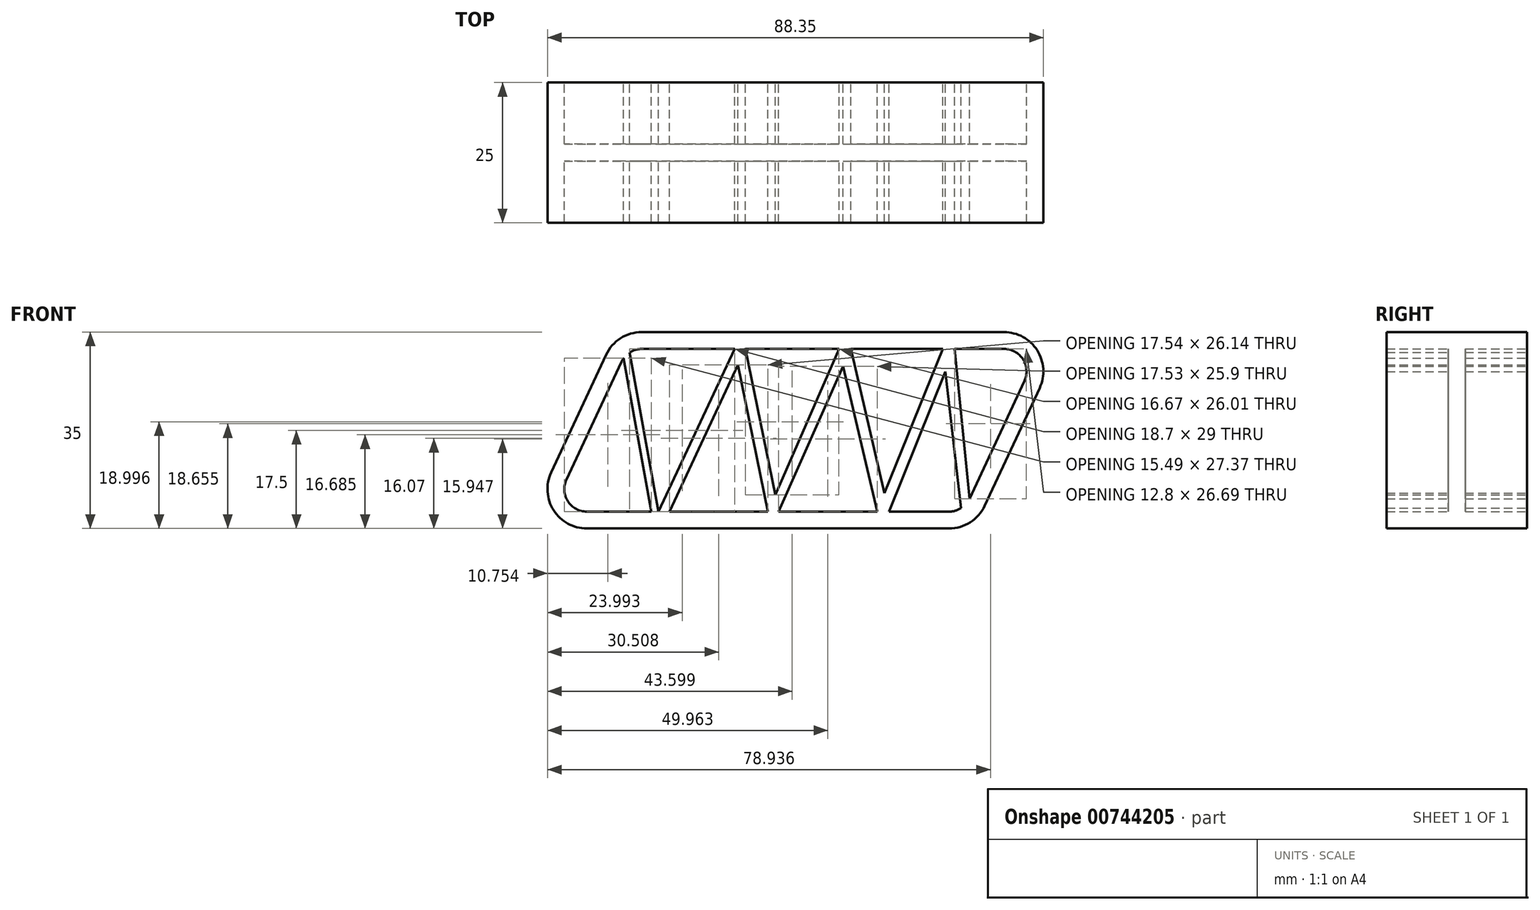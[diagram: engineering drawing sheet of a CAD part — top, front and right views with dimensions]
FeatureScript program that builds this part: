
annotation { "Feature Type Name" : "Feature", "Feature Type Description" : "" }
export const myFeature = defineFeature(function(context is Context, id is Id, definition is map)
    precondition{}
    {
        {
            var Q0;
            Q0=qCreatedBy(makeId("Front.planeOp"),FACE);
            var sketch = newSketch(context, id + "F0", { "sketchPlane" : qUnion([Q0])});
            skLineSegment(sketch, "E0", {"start": v(-27.29, -2) * mm, "end": v(37.26, -2) * mm});
            skLineSegment(sketch, "E1", {"start": v(43.6, 2.04) * mm, "end": v(53.4, 23.04) * mm});
            skLineSegment(sketch, "E2", {"start": v(47.06, 33) * mm, "end": v(-17.5, 33) * mm});
            skLineSegment(sketch, "E3", {"start": v(-23.84, 28.96) * mm, "end": v(-33.63, 7.96) * mm});
            skArc(sketch, "E4.filletArc", {"start": v(-33.63, 7.96) * mm, "mid": v(-33.2, 1.24) * mm, "end": v(-27.29, -2) * mm});
            skArc(sketch, "E5.filletArc", {"start": v(37.26, -2) * mm, "mid": v(41.02, -0.9) * mm, "end": v(43.6, 2.04) * mm});
            skPoint(sketch, "E6.visualSharp", {"position": v(53.33, 32) * mm});
            skPoint(sketch, "E7.visualSharp", {"position": v(58.04, 33) * mm});
            skArc(sketch, "E7.filletArc", {"start": v(53.4, 23.04) * mm, "mid": v(52.96, 29.76) * mm, "end": v(47.06, 33) * mm});
            skPoint(sketch, "E8.visualSharp", {"position": v(-21.96, 33) * mm});
            skArc(sketch, "E8.filletArc", {"start": v(-17.5, 33) * mm, "mid": v(-21.26, 31.9) * mm, "end": v(-23.84, 28.96) * mm});
            skArc(sketch, "E9.0", {"start": v(50.68, 24.3) * mm, "mid": v(50.43, 28.15) * mm, "end": v(47.06, 30) * mm});
            skLineSegment(sketch, "E9.1", {"start": v(40.89, 3.3) * mm, "end": v(50.68, 24.3) * mm});
            skLineSegment(sketch, "E9.2", {"start": v(47.06, 30) * mm, "end": v(38.24, 30) * mm});
            skArc(sketch, "E9.3", {"start": v(37.26, 1) * mm, "mid": v(38.38, 1.16) * mm, "end": v(39.41, 1.63) * mm});
            skArc(sketch, "E9.4", {"start": v(-17.5, 30) * mm, "mid": v(-18.62, 29.84) * mm, "end": v(-19.65, 29.37) * mm});
            skLineSegment(sketch, "E9.5", {"start": v(-21.12, 27.7) * mm, "end": v(-30.91, 6.7) * mm});
            skArc(sketch, "E9.6", {"start": v(-30.91, 6.7) * mm, "mid": v(-30.66, 2.85) * mm, "end": v(-27.29, 1) * mm});
            skLineSegment(sketch, "E9.7", {"start": v(-27.29, 1) * mm, "end": v(-15.8, 1) * mm});
            skLineSegment(sketch, "E10", {"start": v(-19.65, 29.37) * mm, "end": v(-14.54, 1) * mm});
            skLineSegment(sketch, "E11", {"start": v(-14.54, 1) * mm, "end": v(-0.95, 30) * mm});
            skLineSegment(sketch, "E12", {"start": v(-0.36, 27.14) * mm, "end": v(4.99, 1) * mm});
            skLineSegment(sketch, "E13", {"start": v(6.3, 4) * mm, "end": v(17.65, 30) * mm});
            skLineSegment(sketch, "E14", {"start": v(18.37, 26.9) * mm, "end": v(24.44, 1) * mm});
            skLineSegment(sketch, "E15", {"start": v(25.77, 4.3) * mm, "end": v(36.14, 30) * mm});
            skLineSegment(sketch, "E16", {"start": v(36.6, 25.95) * mm, "end": v(39.41, 1.63) * mm});
            skLineSegment(sketch, "E17", {"start": v(-15.8, 1) * mm, "end": v(-20.72, 28.37) * mm});
            skLineSegment(sketch, "E18", {"start": v(-12.55, 1) * mm, "end": v(-0.36, 27.14) * mm});
            skLineSegment(sketch, "E19", {"start": v(0.97, 30) * mm, "end": v(6.3, 4) * mm});
            skLineSegment(sketch, "E20", {"start": v(6.9, 1) * mm, "end": v(18.37, 26.9) * mm});
            skLineSegment(sketch, "E21", {"start": v(19.75, 30) * mm, "end": v(25.77, 4.3) * mm});
            skLineSegment(sketch, "E22", {"start": v(26.54, 1) * mm, "end": v(36.6, 25.95) * mm});
            skLineSegment(sketch, "E23", {"start": v(38.24, 30) * mm, "end": v(40.89, 3.3) * mm});
            skArc(sketch, "E24.trimOffspring", {"start": v(-20.72, 28.37) * mm, "mid": v(-20.94, 28.04) * mm, "end": v(-21.12, 27.7) * mm});
            skLineSegment(sketch, "E25.trimOffspring", {"start": v(-12.55, 1) * mm, "end": v(4.99, 1) * mm});
            skLineSegment(sketch, "E26.trimOffspring", {"start": v(-0.95, 30) * mm, "end": v(-17.5, 30) * mm});
            skLineSegment(sketch, "E27.trimOffspring", {"start": v(6.9, 1) * mm, "end": v(24.44, 1) * mm});
            skLineSegment(sketch, "E28.trimOffspring", {"start": v(26.54, 1) * mm, "end": v(37.26, 1) * mm});
            skLineSegment(sketch, "E29.trimOffspring", {"start": v(36.14, 30) * mm, "end": v(19.75, 30) * mm});
            skLineSegment(sketch, "E30.trimOffspring", {"start": v(17.65, 30) * mm, "end": v(0.97, 30) * mm});
            skSolve(sketch);
        }
        {
            var Q0;
            Q0 = qSketchRegion(id + "F0", true);
            extrude(context, id + "F1", {"entities" : qUnion([Q0]), "depth" : 25 * mm, "offsetDistance" : 25 * mm});
        }
        {
            var Q0;
            Q0=qCreatedBy(makeId("Front.planeOp"),FACE);
            cPlane(context, id + "F2", {"entities" : qUnion([Q0]), "cplaneType" : CPlaneType.OFFSET, "offset" : 12.5 * mm, "width" : 150 * mm, "height" : 150 * mm});
        }
        {
            var Q0;
            Q0=qCreatedBy(id+"F2.planeOp",FACE);
            var sketch = newSketch(context, id + "F3", { "sketchPlane" : qUnion([Q0])});
            skLineSegment(sketch, "E31", {"start": v(-29, -0.64) * mm, "end": v(-32.5, 4.62) * mm});
            skLineSegment(sketch, "E32", {"start": v(-32.5, 4.62) * mm, "end": v(-21.06, 30.1) * mm});
            skLineSegment(sketch, "E33", {"start": v(-21.06, 30.1) * mm, "end": v(-16.46, 31.9) * mm});
            skLineSegment(sketch, "E34", {"start": v(-16.46, 31.9) * mm, "end": v(46.62, 31.9) * mm});
            skLineSegment(sketch, "E35", {"start": v(46.62, 31.9) * mm, "end": v(50.54, 29.76) * mm});
            skLineSegment(sketch, "E36", {"start": v(50.54, 29.76) * mm, "end": v(52.68, 25.83) * mm});
            skLineSegment(sketch, "E37", {"start": v(52.68, 25.83) * mm, "end": v(49.98, 17.87) * mm});
            skLineSegment(sketch, "E38", {"start": v(49.98, 17.87) * mm, "end": v(40.22, 0) * mm});
            skLineSegment(sketch, "E39", {"start": v(40.22, 0) * mm, "end": v(-29, -0.64) * mm});
            skSolve(sketch);
        }
        {
            var Q0;
            Q0 = qSketchRegion(id + "F3", true);
            extrude(context, id + "F4", {"entities" : qUnion([Q0]), "operationType" : NewBodyOperationType.ADD, "endBound" : BoundingType.SYMMETRIC, "depth" : 3 * mm, "offsetDistance" : 25 * mm});
        }
    });
